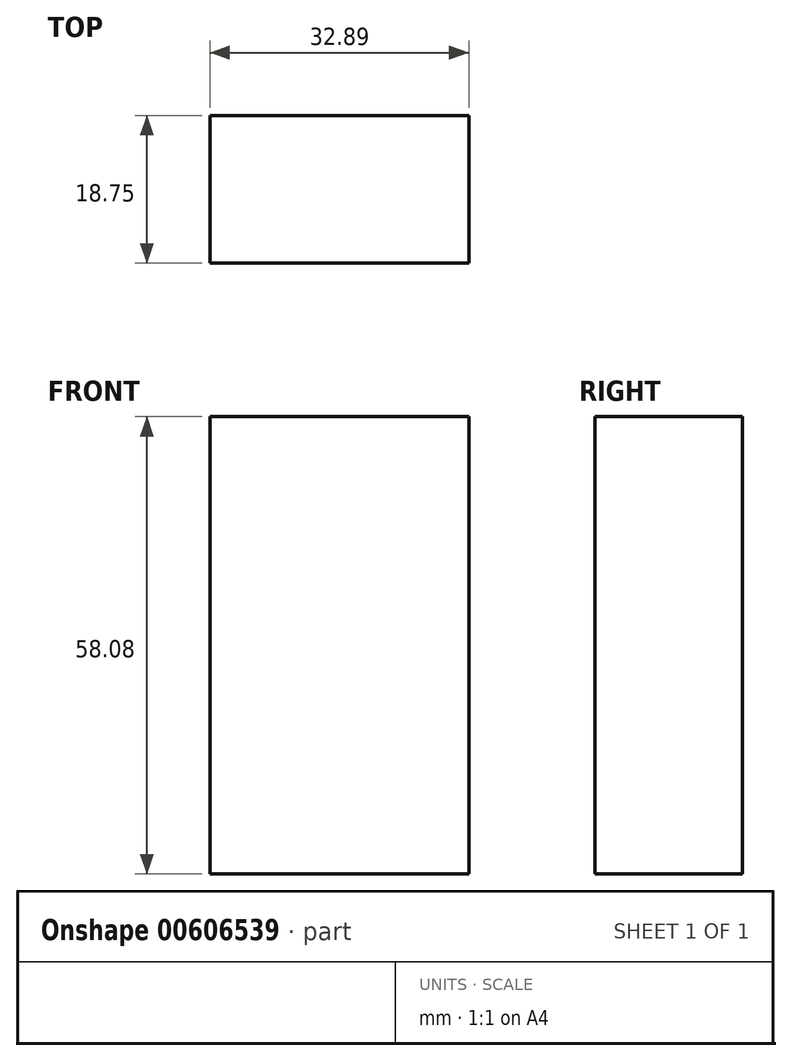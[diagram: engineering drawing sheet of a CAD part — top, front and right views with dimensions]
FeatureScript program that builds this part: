
annotation { "Feature Type Name" : "Feature", "Feature Type Description" : "" }
export const myFeature = defineFeature(function(context is Context, id is Id, definition is map)
    precondition{}
    {
        {
            var Q0;
            Q0=qCreatedBy(makeId("Front.planeOp"),FACE);
            var sketch = newSketch(context, id + "F0", { "sketchPlane" : qUnion([Q0])});
            skLineSegment(sketch, "E0", {"start": v(32.89, 0) * mm, "end": v(32.89, 58.08) * mm});
            skLineSegment(sketch, "E1", {"start": v(0, 0) * mm, "end": v(0, 58.08) * mm});
            skLineSegment(sketch, "E2", {"start": v(0, 58.08) * mm, "end": v(32.89, 58.08) * mm});
            skLineSegment(sketch, "E3", {"start": v(32.89, 0) * mm, "end": v(0, 0) * mm});
            skSolve(sketch);
        }
        {
            var Q0;
            Q0 = qSketchRegion(id + "F0", true);
            extrude(context, id + "F1", {"entities" : qUnion([Q0]), "depth" : 18.75 * mm, "offsetDistance" : 25.4 * mm});
        }
    });
